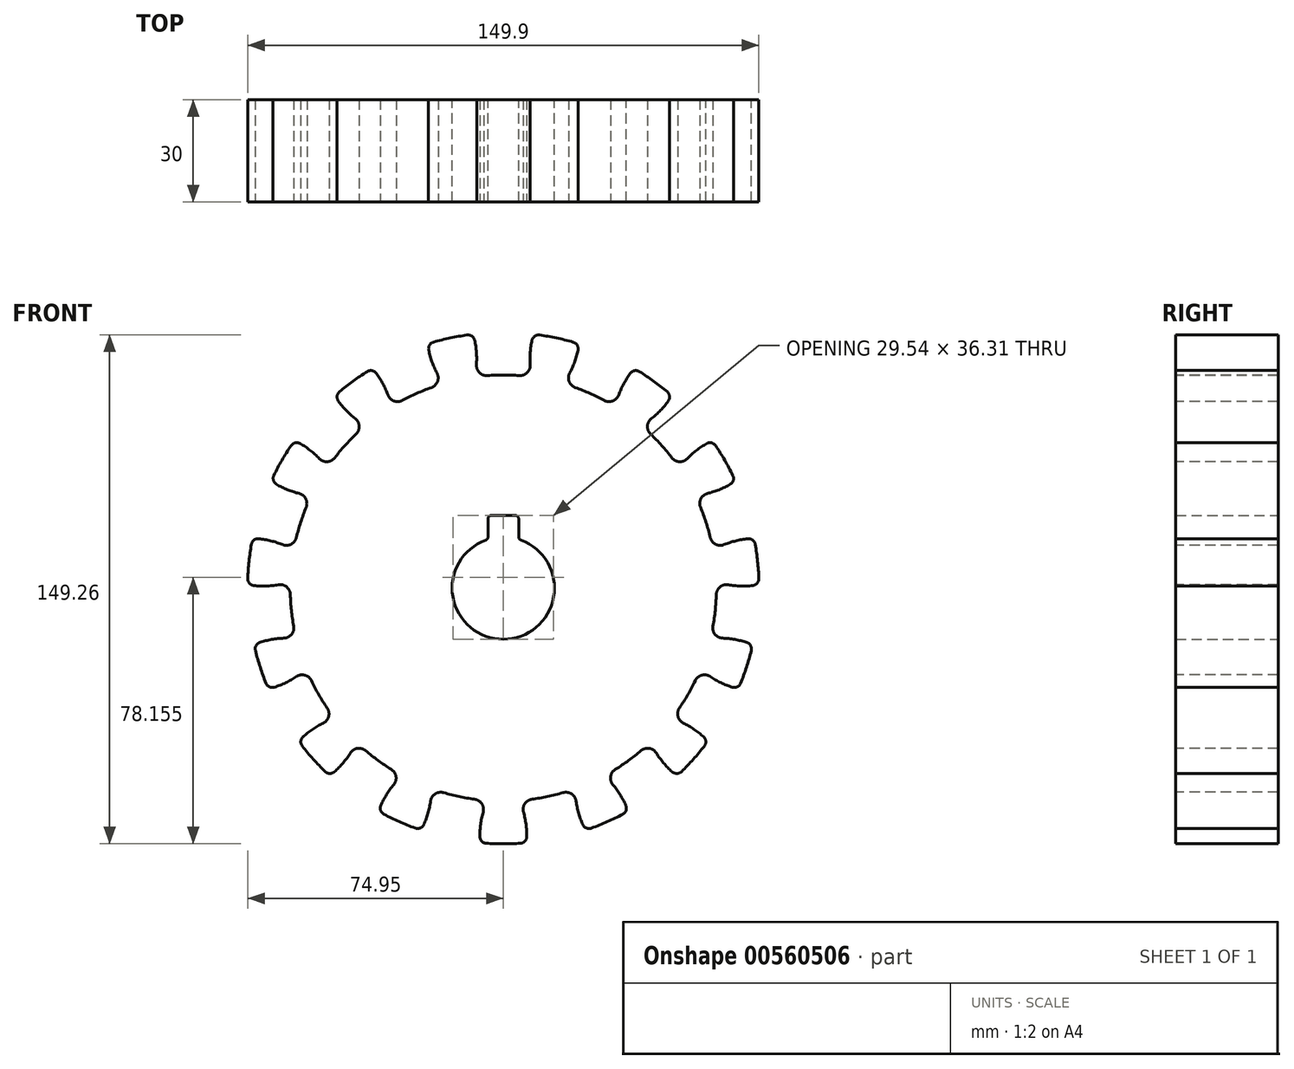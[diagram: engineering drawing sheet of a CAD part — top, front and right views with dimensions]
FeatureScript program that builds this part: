
annotation { "Feature Type Name" : "Feature", "Feature Type Description" : "" }
export const myFeature = defineFeature(function(context is Context, id is Id, definition is map)
    precondition{}
    {
        {
            var Q0;
            Q0=qCreatedBy(makeId("Front.planeOp"),FACE);
            var sketch = newSketch(context, id + "F0", { "sketchPlane" : qUnion([Q0])});
            skCircle(sketch, "E0", {"center": v(0, 0) * mm, "radius": 75 * mm});
            skArc(sketch, "E1", {"start": v(-5.16, 14.09) * mm, "mid": v(0, -15) * mm, "end": v(5.16, 14.09) * mm});
            skLineSegment(sketch, "E2.top", {"start": v(-3.5, 21.3) * mm, "end": v(3.5, 21.3) * mm});
            skLineSegment(sketch, "E2.left", {"start": v(-4.5, 15.02) * mm, "end": v(-4.5, 20.3) * mm});
            skLineSegment(sketch, "E2.right", {"start": v(4.5, 15.02) * mm, "end": v(4.5, 20.3) * mm});
            skPoint(sketch, "E3.visualSharp", {"position": v(-4.5, 21.3) * mm});
            skArc(sketch, "E3.filletArc", {"start": v(-3.5, 21.3) * mm, "mid": v(-4.2, 21.02) * mm, "end": v(-4.5, 20.3) * mm});
            skPoint(sketch, "E4.visualSharp", {"position": v(4.5, 21.3) * mm});
            skArc(sketch, "E4.filletArc", {"start": v(4.5, 20.3) * mm, "mid": v(4.2, 21.02) * mm, "end": v(3.5, 21.3) * mm});
            skPoint(sketch, "E5.visualSharp", {"position": v(4.5, 14.3) * mm});
            skArc(sketch, "E5.filletArc", {"start": v(4.5, 15.02) * mm, "mid": v(4.68, 14.45) * mm, "end": v(5.16, 14.09) * mm});
            skPoint(sketch, "E6.visualSharp", {"position": v(-4.5, 14.3) * mm});
            skArc(sketch, "E6.filletArc", {"start": v(-5.16, 14.09) * mm, "mid": v(-4.68, 14.45) * mm, "end": v(-4.5, 15.02) * mm});
            skSolve(sketch);
        }
        {
            var Q0;
            Q0 = qSketchRegion(id + "F0", true);
            extrude(context, id + "F1", {"entities" : qUnion([Q0]), "depth" : 30 * mm, "offsetDistance" : 25 * mm});
        }
        {
            var Q0;
            Q0=makeQuery(id+"F1.opExtrude","CAP_FACE",FACE,{"disambiguationData":[OSD([sQuery(id+"F0.wireOp",EDGE,"E0"),sQuery(id+"F0.wireOp",EDGE,"E1"),sQuery(id+"F0.wireOp",EDGE,"E2.top"),sQuery(id+"F0.wireOp",EDGE,"E2.left"),sQuery(id+"F0.wireOp",EDGE,"E2.right"),sQuery(id+"F0.wireOp",EDGE,"E3.filletArc"),sQuery(id+"F0.wireOp",EDGE,"E4.filletArc"),sQuery(id+"F0.wireOp",EDGE,"E5.filletArc"),sQuery(id+"F0.wireOp",EDGE,"E6.filletArc")])],"isStart":false});
            var sketch = newSketch(context, id + "F2", { "sketchPlane" : qUnion([Q0])});
            skArc(sketch, "E7", {"start": v(16.1, 86) * mm, "mid": v(0, 87.5) * mm, "end": v(-16.1, 86) * mm});
            skArc(sketch, "E8", {"start": v(4.66, 62.33) * mm, "mid": v(0, 62.5) * mm, "end": v(-4.66, 62.33) * mm});
            skPoint(sketch, "E9", {"position": v(0, 68.35) * mm});
            skArc(sketch, "E10", {"start": v(16.1, 86) * mm, "mid": v(9.63, 76.71) * mm, "end": v(7.88, 65.53) * mm});
            skArc(sketch, "E11.trimOffspring", {"start": v(-16.1, 86) * mm, "mid": v(-9.63, 76.71) * mm, "end": v(-7.88, 65.53) * mm});
            skPoint(sketch, "E12.visualSharp", {"position": v(-8.4, 61.93) * mm});
            skArc(sketch, "E12.filletArc", {"start": v(-7.88, 65.53) * mm, "mid": v(-7, 63.2) * mm, "end": v(-4.66, 62.33) * mm});
            skPoint(sketch, "E13.visualSharp", {"position": v(8.4, 61.93) * mm});
            skArc(sketch, "E13.filletArc", {"start": v(4.66, 62.33) * mm, "mid": v(7, 63.2) * mm, "end": v(7.88, 65.53) * mm});
            skArc(sketch, "E14.1.0", {"start": v(-20.28, 85.12) * mm, "mid": v(-35.59, 79.94) * mm, "end": v(-49.68, 72.03) * mm});
            skArc(sketch, "E14.1.1", {"start": v(-49.68, 72.03) * mm, "mid": v(-40, 66.16) * mm, "end": v(-33.85, 56.66) * mm});
            skArc(sketch, "E14.1.2", {"start": v(-20.28, 85.12) * mm, "mid": v(-22.4, 74) * mm, "end": v(-19.45, 63.07) * mm});
            skArc(sketch, "E14.1.3", {"start": v(-21.09, 58.83) * mm, "mid": v(-19.3, 60.58) * mm, "end": v(-19.45, 63.07) * mm});
            skArc(sketch, "E14.1.4", {"start": v(-21.09, 58.83) * mm, "mid": v(-25.42, 57.1) * mm, "end": v(-29.61, 55.04) * mm});
            skArc(sketch, "E14.1.5", {"start": v(-33.85, 56.66) * mm, "mid": v(-32.1, 54.88) * mm, "end": v(-29.61, 55.04) * mm});
            skArc(sketch, "E14.2.0", {"start": v(-53.15, 69.5) * mm, "mid": v(-65.03, 58.55) * mm, "end": v(-74.68, 45.6) * mm});
            skArc(sketch, "E14.2.1", {"start": v(-74.68, 45.6) * mm, "mid": v(-63.45, 44.17) * mm, "end": v(-53.97, 38) * mm});
            skArc(sketch, "E14.2.2", {"start": v(-53.15, 69.5) * mm, "mid": v(-50.56, 58.49) * mm, "end": v(-43.42, 49.7) * mm});
            skArc(sketch, "E14.2.3", {"start": v(-43.2, 45.17) * mm, "mid": v(-42.27, 47.49) * mm, "end": v(-43.42, 49.7) * mm});
            skArc(sketch, "E14.2.4", {"start": v(-43.2, 45.17) * mm, "mid": v(-46.45, 41.82) * mm, "end": v(-49.44, 38.24) * mm});
            skArc(sketch, "E14.2.5", {"start": v(-53.97, 38) * mm, "mid": v(-51.65, 37.08) * mm, "end": v(-49.44, 38.24) * mm});
            skArc(sketch, "E15.3.3.0", {"start": v(-76.82, 41.88) * mm, "mid": v(-83.22, 27.04) * mm, "end": v(-86.77, 11.27) * mm});
            skArc(sketch, "E15.4.3.0", {"start": v(-86.77, 11.27) * mm, "mid": v(-75.93, 14.54) * mm, "end": v(-64.76, 12.75) * mm});
            skArc(sketch, "E15.8.3.0", {"start": v(-76.82, 41.88) * mm, "mid": v(-69.98, 32.87) * mm, "end": v(-59.89, 27.74) * mm});
            skArc(sketch, "E15.12.3.0", {"start": v(-57.83, 23.7) * mm, "mid": v(-57.93, 26.19) * mm, "end": v(-59.89, 27.74) * mm});
            skArc(sketch, "E15.16.3.0", {"start": v(-57.83, 23.7) * mm, "mid": v(-59.44, 19.31) * mm, "end": v(-60.72, 14.82) * mm});
            skArc(sketch, "E15.20.3.0", {"start": v(-64.76, 12.75) * mm, "mid": v(-62.26, 12.87) * mm, "end": v(-60.72, 14.82) * mm});
            skArc(sketch, "E16.3.4.0", {"start": v(-87.22, 7.01) * mm, "mid": v(-87.02, -9.15) * mm, "end": v(-83.85, -25) * mm});
            skArc(sketch, "E16.4.4.0", {"start": v(-83.85, -25) * mm, "mid": v(-75.28, -17.6) * mm, "end": v(-64.35, -14.69) * mm});
            skArc(sketch, "E16.8.4.0", {"start": v(-87.22, 7.01) * mm, "mid": v(-77.3, 1.56) * mm, "end": v(-66, 0.99) * mm});
            skArc(sketch, "E16.12.4.0", {"start": v(-62.47, -1.88) * mm, "mid": v(-63.58, 0.36) * mm, "end": v(-66, 0.99) * mm});
            skArc(sketch, "E16.16.4.0", {"start": v(-62.47, -1.88) * mm, "mid": v(-62.16, -6.53) * mm, "end": v(-61.5, -11.15) * mm});
            skArc(sketch, "E16.20.4.0", {"start": v(-64.35, -14.69) * mm, "mid": v(-62.11, -13.57) * mm, "end": v(-61.5, -11.15) * mm});
            skArc(sketch, "E16.3.5.0", {"start": v(-82.53, -29.07) * mm, "mid": v(-75.78, -43.75) * mm, "end": v(-66.44, -56.94) * mm});
            skArc(sketch, "E16.4.5.0", {"start": v(-66.44, -56.94) * mm, "mid": v(-61.62, -46.7) * mm, "end": v(-52.8, -39.59) * mm});
            skArc(sketch, "E16.8.5.0", {"start": v(-82.53, -29.07) * mm, "mid": v(-71.25, -30.01) * mm, "end": v(-60.69, -25.94) * mm});
            skArc(sketch, "E16.12.5.0", {"start": v(-56.3, -27.12) * mm, "mid": v(-58.23, -25.53) * mm, "end": v(-60.69, -25.94) * mm});
            skArc(sketch, "E16.16.5.0", {"start": v(-56.3, -27.12) * mm, "mid": v(-54.13, -31.25) * mm, "end": v(-51.64, -35.2) * mm});
            skArc(sketch, "E16.20.5.0", {"start": v(-52.8, -39.59) * mm, "mid": v(-51.22, -37.66) * mm, "end": v(-51.64, -35.2) * mm});
            skArc(sketch, "E16.3.6.0", {"start": v(-63.57, -60.12) * mm, "mid": v(-51.43, -70.79) * mm, "end": v(-37.53, -79.04) * mm});
            skArc(sketch, "E16.4.6.0", {"start": v(-37.53, -79.04) * mm, "mid": v(-37.3, -67.72) * mm, "end": v(-32.14, -57.64) * mm});
            skArc(sketch, "E16.8.6.0", {"start": v(-63.57, -60.12) * mm, "mid": v(-52.88, -56.4) * mm, "end": v(-44.9, -48.38) * mm});
            skArc(sketch, "E16.12.6.0", {"start": v(-40.4, -47.68) * mm, "mid": v(-42.8, -47) * mm, "end": v(-44.9, -48.38) * mm});
            skArc(sketch, "E16.16.6.0", {"start": v(-40.4, -47.68) * mm, "mid": v(-36.74, -50.56) * mm, "end": v(-32.86, -53.16) * mm});
            skArc(sketch, "E16.20.6.0", {"start": v(-32.14, -57.64) * mm, "mid": v(-31.48, -55.24) * mm, "end": v(-32.86, -53.16) * mm});
            skArc(sketch, "E16.3.7.0", {"start": v(-33.62, -80.78) * mm, "mid": v(-18.2, -85.59) * mm, "end": v(-2.14, -87.47) * mm});
            skArc(sketch, "E16.4.7.0", {"start": v(-2.14, -87.47) * mm, "mid": v(-6.52, -77.04) * mm, "end": v(-5.92, -65.73) * mm});
            skArc(sketch, "E16.8.7.0", {"start": v(-33.62, -80.78) * mm, "mid": v(-25.37, -73.03) * mm, "end": v(-21.33, -62.46) * mm});
            skArc(sketch, "E16.12.7.0", {"start": v(-17.52, -60) * mm, "mid": v(-19.99, -60.35) * mm, "end": v(-21.33, -62.46) * mm});
            skArc(sketch, "E16.16.7.0", {"start": v(-17.52, -60) * mm, "mid": v(-13, -61.13) * mm, "end": v(-8.4, -61.93) * mm});
            skArc(sketch, "E16.20.7.0", {"start": v(-5.92, -65.73) * mm, "mid": v(-6.29, -63.27) * mm, "end": v(-8.4, -61.93) * mm});
            skArc(sketch, "E16.3.8.0", {"start": v(2.14, -87.47) * mm, "mid": v(18.2, -85.59) * mm, "end": v(33.62, -80.78) * mm});
            skArc(sketch, "E16.4.8.0", {"start": v(33.62, -80.78) * mm, "mid": v(25.37, -73.03) * mm, "end": v(21.33, -62.46) * mm});
            skArc(sketch, "E16.8.8.0", {"start": v(2.14, -87.47) * mm, "mid": v(6.52, -77.04) * mm, "end": v(5.92, -65.73) * mm});
            skArc(sketch, "E16.12.8.0", {"start": v(8.4, -61.93) * mm, "mid": v(6.29, -63.27) * mm, "end": v(5.92, -65.73) * mm});
            skArc(sketch, "E16.16.8.0", {"start": v(8.4, -61.93) * mm, "mid": v(13, -61.13) * mm, "end": v(17.52, -60) * mm});
            skArc(sketch, "E16.20.8.0", {"start": v(21.33, -62.46) * mm, "mid": v(19.99, -60.35) * mm, "end": v(17.52, -60) * mm});
            skArc(sketch, "E16.3.9.0", {"start": v(37.53, -79.04) * mm, "mid": v(51.43, -70.79) * mm, "end": v(63.57, -60.12) * mm});
            skArc(sketch, "E16.4.9.0", {"start": v(63.57, -60.12) * mm, "mid": v(52.88, -56.4) * mm, "end": v(44.9, -48.38) * mm});
            skArc(sketch, "E16.8.9.0", {"start": v(37.53, -79.04) * mm, "mid": v(37.3, -67.72) * mm, "end": v(32.14, -57.64) * mm});
            skArc(sketch, "E16.12.9.0", {"start": v(32.86, -53.16) * mm, "mid": v(31.48, -55.24) * mm, "end": v(32.14, -57.64) * mm});
            skArc(sketch, "E16.16.9.0", {"start": v(32.86, -53.16) * mm, "mid": v(36.74, -50.56) * mm, "end": v(40.4, -47.68) * mm});
            skArc(sketch, "E16.20.9.0", {"start": v(44.9, -48.38) * mm, "mid": v(42.8, -47) * mm, "end": v(40.4, -47.68) * mm});
            skArc(sketch, "E16.3.10.0", {"start": v(66.44, -56.94) * mm, "mid": v(75.78, -43.75) * mm, "end": v(82.53, -29.07) * mm});
            skArc(sketch, "E16.4.10.0", {"start": v(82.53, -29.07) * mm, "mid": v(71.25, -30.01) * mm, "end": v(60.69, -25.94) * mm});
            skArc(sketch, "E16.8.10.0", {"start": v(66.44, -56.94) * mm, "mid": v(61.62, -46.7) * mm, "end": v(52.8, -39.59) * mm});
            skArc(sketch, "E16.12.10.0", {"start": v(51.64, -35.2) * mm, "mid": v(51.22, -37.66) * mm, "end": v(52.8, -39.59) * mm});
            skArc(sketch, "E16.16.10.0", {"start": v(51.64, -35.2) * mm, "mid": v(54.13, -31.25) * mm, "end": v(56.3, -27.12) * mm});
            skArc(sketch, "E16.20.10.0", {"start": v(60.69, -25.94) * mm, "mid": v(58.23, -25.53) * mm, "end": v(56.3, -27.12) * mm});
            skArc(sketch, "E16.3.11.0", {"start": v(83.85, -25) * mm, "mid": v(87.02, -9.15) * mm, "end": v(87.22, 7.01) * mm});
            skArc(sketch, "E16.4.11.0", {"start": v(87.22, 7.01) * mm, "mid": v(77.3, 1.56) * mm, "end": v(66, 0.99) * mm});
            skArc(sketch, "E16.8.11.0", {"start": v(83.85, -25) * mm, "mid": v(75.28, -17.6) * mm, "end": v(64.35, -14.69) * mm});
            skArc(sketch, "E16.12.11.0", {"start": v(61.5, -11.15) * mm, "mid": v(62.11, -13.57) * mm, "end": v(64.35, -14.69) * mm});
            skArc(sketch, "E16.16.11.0", {"start": v(61.5, -11.15) * mm, "mid": v(62.16, -6.53) * mm, "end": v(62.47, -1.88) * mm});
            skArc(sketch, "E16.20.11.0", {"start": v(66, 0.99) * mm, "mid": v(63.58, 0.36) * mm, "end": v(62.47, -1.88) * mm});
            skArc(sketch, "E16.3.12.0", {"start": v(86.77, 11.27) * mm, "mid": v(83.22, 27.04) * mm, "end": v(76.82, 41.88) * mm});
            skArc(sketch, "E16.4.12.0", {"start": v(76.82, 41.88) * mm, "mid": v(69.98, 32.87) * mm, "end": v(59.89, 27.74) * mm});
            skArc(sketch, "E16.8.12.0", {"start": v(86.77, 11.27) * mm, "mid": v(75.93, 14.54) * mm, "end": v(64.76, 12.75) * mm});
            skArc(sketch, "E16.12.12.0", {"start": v(60.72, 14.82) * mm, "mid": v(62.26, 12.87) * mm, "end": v(64.76, 12.75) * mm});
            skArc(sketch, "E16.16.12.0", {"start": v(60.72, 14.82) * mm, "mid": v(59.44, 19.31) * mm, "end": v(57.83, 23.7) * mm});
            skArc(sketch, "E16.20.12.0", {"start": v(59.89, 27.74) * mm, "mid": v(57.93, 26.19) * mm, "end": v(57.83, 23.7) * mm});
            skArc(sketch, "E16.3.13.0", {"start": v(74.68, 45.6) * mm, "mid": v(65.03, 58.55) * mm, "end": v(53.15, 69.5) * mm});
            skArc(sketch, "E16.4.13.0", {"start": v(53.15, 69.5) * mm, "mid": v(50.56, 58.49) * mm, "end": v(43.42, 49.7) * mm});
            skArc(sketch, "E16.8.13.0", {"start": v(74.68, 45.6) * mm, "mid": v(63.45, 44.17) * mm, "end": v(53.97, 38) * mm});
            skArc(sketch, "E16.12.13.0", {"start": v(49.44, 38.24) * mm, "mid": v(51.65, 37.08) * mm, "end": v(53.97, 38) * mm});
            skArc(sketch, "E16.16.13.0", {"start": v(49.44, 38.24) * mm, "mid": v(46.45, 41.82) * mm, "end": v(43.2, 45.17) * mm});
            skArc(sketch, "E16.20.13.0", {"start": v(43.42, 49.7) * mm, "mid": v(42.27, 47.49) * mm, "end": v(43.2, 45.17) * mm});
            skArc(sketch, "E16.3.14.0", {"start": v(49.68, 72.03) * mm, "mid": v(35.59, 79.94) * mm, "end": v(20.28, 85.12) * mm});
            skArc(sketch, "E16.4.14.0", {"start": v(20.28, 85.12) * mm, "mid": v(22.4, 74) * mm, "end": v(19.45, 63.07) * mm});
            skArc(sketch, "E16.8.14.0", {"start": v(49.68, 72.03) * mm, "mid": v(40, 66.16) * mm, "end": v(33.85, 56.66) * mm});
            skArc(sketch, "E16.12.14.0", {"start": v(29.61, 55.04) * mm, "mid": v(32.1, 54.88) * mm, "end": v(33.85, 56.66) * mm});
            skArc(sketch, "E16.16.14.0", {"start": v(29.61, 55.04) * mm, "mid": v(25.42, 57.1) * mm, "end": v(21.09, 58.83) * mm});
            skArc(sketch, "E16.20.14.0", {"start": v(19.45, 63.07) * mm, "mid": v(19.3, 60.58) * mm, "end": v(21.09, 58.83) * mm});
            skSolve(sketch);
        }
        {
            var Q0;
            Q0 = qSketchRegion(id + "F2", true);
            extrude(context, id + "F3", {"entities" : qUnion([Q0]), "operationType" : NewBodyOperationType.REMOVE, "oppositeDirection" : true, "depth" : 31 * mm, "offsetDistance" : 25 * mm});
        }
        {
            var Q0;
            Q0=makeQuery(id+"F3.boolean.opBoolean","INTERSECT",EDGE,{"derivedFrom":[makeQuery(id+"F1.opExtrude","SWEPT_FACE",FACE,{"disambiguationData":[OSD([sQuery(id+"F0.wireOp",EDGE,"E0")])]}),makeQuery(id+"F3.opExtrude","SWEPT_FACE",FACE,{"disambiguationData":[OSD([sQuery(id+"F2.wireOp",EDGE,"E16.4.12.0")])]})]});
            var Q1;
            Q1=makeQuery(id+"F3.boolean.opBoolean","INTERSECT",EDGE,{"derivedFrom":[makeQuery(id+"F1.opExtrude","SWEPT_FACE",FACE,{"disambiguationData":[OSD([sQuery(id+"F0.wireOp",EDGE,"E0")])]}),makeQuery(id+"F3.opExtrude","SWEPT_FACE",FACE,{"disambiguationData":[OSD([sQuery(id+"F2.wireOp",EDGE,"E16.8.13.0")])]})]});
            var Q2;
            Q2=makeQuery(id+"F3.boolean.opBoolean","INTERSECT",EDGE,{"derivedFrom":[makeQuery(id+"F1.opExtrude","SWEPT_FACE",FACE,{"disambiguationData":[OSD([sQuery(id+"F0.wireOp",EDGE,"E0")])]}),makeQuery(id+"F3.opExtrude","SWEPT_FACE",FACE,{"disambiguationData":[OSD([sQuery(id+"F2.wireOp",EDGE,"E16.4.13.0")])]})]});
            var Q3;
            Q3=makeQuery(id+"F3.boolean.opBoolean","INTERSECT",EDGE,{"derivedFrom":[makeQuery(id+"F1.opExtrude","SWEPT_FACE",FACE,{"disambiguationData":[OSD([sQuery(id+"F0.wireOp",EDGE,"E0")])]}),makeQuery(id+"F3.opExtrude","SWEPT_FACE",FACE,{"disambiguationData":[OSD([sQuery(id+"F2.wireOp",EDGE,"E16.8.14.0")])]})]});
            var Q4;
            Q4=makeQuery(id+"F3.boolean.opBoolean","INTERSECT",EDGE,{"derivedFrom":[makeQuery(id+"F1.opExtrude","SWEPT_FACE",FACE,{"disambiguationData":[OSD([sQuery(id+"F0.wireOp",EDGE,"E0")])]}),makeQuery(id+"F3.opExtrude","SWEPT_FACE",FACE,{"disambiguationData":[OSD([sQuery(id+"F2.wireOp",EDGE,"E16.4.14.0")])]})]});
            var Q5;
            Q5=makeQuery(id+"F3.boolean.opBoolean","INTERSECT",EDGE,{"derivedFrom":[makeQuery(id+"F1.opExtrude","SWEPT_FACE",FACE,{"disambiguationData":[OSD([sQuery(id+"F0.wireOp",EDGE,"E0")])]}),makeQuery(id+"F3.opExtrude","SWEPT_FACE",FACE,{"disambiguationData":[OSD([sQuery(id+"F2.wireOp",EDGE,"E10")])]})]});
            var Q6;
            Q6=makeQuery(id+"F3.boolean.opBoolean","INTERSECT",EDGE,{"derivedFrom":[makeQuery(id+"F1.opExtrude","SWEPT_FACE",FACE,{"disambiguationData":[OSD([sQuery(id+"F0.wireOp",EDGE,"E0")])]}),makeQuery(id+"F3.opExtrude","SWEPT_FACE",FACE,{"disambiguationData":[OSD([sQuery(id+"F2.wireOp",EDGE,"E11.trimOffspring")])]})]});
            var Q7;
            Q7=makeQuery(id+"F3.boolean.opBoolean","INTERSECT",EDGE,{"derivedFrom":[makeQuery(id+"F1.opExtrude","SWEPT_FACE",FACE,{"disambiguationData":[OSD([sQuery(id+"F0.wireOp",EDGE,"E0")])]}),makeQuery(id+"F3.opExtrude","SWEPT_FACE",FACE,{"disambiguationData":[OSD([sQuery(id+"F2.wireOp",EDGE,"E14.1.2")])]})]});
            var Q8;
            Q8=makeQuery(id+"F3.boolean.opBoolean","INTERSECT",EDGE,{"derivedFrom":[makeQuery(id+"F1.opExtrude","SWEPT_FACE",FACE,{"disambiguationData":[OSD([sQuery(id+"F0.wireOp",EDGE,"E0")])]}),makeQuery(id+"F3.opExtrude","SWEPT_FACE",FACE,{"disambiguationData":[OSD([sQuery(id+"F2.wireOp",EDGE,"E14.1.1")])]})]});
            var Q9;
            Q9=makeQuery(id+"F3.boolean.opBoolean","INTERSECT",EDGE,{"derivedFrom":[makeQuery(id+"F1.opExtrude","SWEPT_FACE",FACE,{"disambiguationData":[OSD([sQuery(id+"F0.wireOp",EDGE,"E0")])]}),makeQuery(id+"F3.opExtrude","SWEPT_FACE",FACE,{"disambiguationData":[OSD([sQuery(id+"F2.wireOp",EDGE,"E14.2.2")])]})]});
            var Q10;
            Q10=makeQuery(id+"F3.boolean.opBoolean","INTERSECT",EDGE,{"derivedFrom":[makeQuery(id+"F1.opExtrude","SWEPT_FACE",FACE,{"disambiguationData":[OSD([sQuery(id+"F0.wireOp",EDGE,"E0")])]}),makeQuery(id+"F3.opExtrude","SWEPT_FACE",FACE,{"disambiguationData":[OSD([sQuery(id+"F2.wireOp",EDGE,"E14.2.1")])]})]});
            var Q11;
            Q11=makeQuery(id+"F3.boolean.opBoolean","INTERSECT",EDGE,{"derivedFrom":[makeQuery(id+"F1.opExtrude","SWEPT_FACE",FACE,{"disambiguationData":[OSD([sQuery(id+"F0.wireOp",EDGE,"E0")])]}),makeQuery(id+"F3.opExtrude","SWEPT_FACE",FACE,{"disambiguationData":[OSD([sQuery(id+"F2.wireOp",EDGE,"E15.8.3.0")])]})]});
            var Q12;
            Q12=makeQuery(id+"F3.boolean.opBoolean","INTERSECT",EDGE,{"derivedFrom":[makeQuery(id+"F1.opExtrude","SWEPT_FACE",FACE,{"disambiguationData":[OSD([sQuery(id+"F0.wireOp",EDGE,"E0")])]}),makeQuery(id+"F3.opExtrude","SWEPT_FACE",FACE,{"disambiguationData":[OSD([sQuery(id+"F2.wireOp",EDGE,"E15.4.3.0")])]})]});
            var Q13;
            Q13=makeQuery(id+"F3.boolean.opBoolean","INTERSECT",EDGE,{"derivedFrom":[makeQuery(id+"F1.opExtrude","SWEPT_FACE",FACE,{"disambiguationData":[OSD([sQuery(id+"F0.wireOp",EDGE,"E0")])]}),makeQuery(id+"F3.opExtrude","SWEPT_FACE",FACE,{"disambiguationData":[OSD([sQuery(id+"F2.wireOp",EDGE,"E16.8.4.0")])]})]});
            var Q14;
            Q14=makeQuery(id+"F3.boolean.opBoolean","INTERSECT",EDGE,{"derivedFrom":[makeQuery(id+"F1.opExtrude","SWEPT_FACE",FACE,{"disambiguationData":[OSD([sQuery(id+"F0.wireOp",EDGE,"E0")])]}),makeQuery(id+"F3.opExtrude","SWEPT_FACE",FACE,{"disambiguationData":[OSD([sQuery(id+"F2.wireOp",EDGE,"E16.4.4.0")])]})]});
            var Q15;
            Q15=makeQuery(id+"F3.boolean.opBoolean","INTERSECT",EDGE,{"derivedFrom":[makeQuery(id+"F1.opExtrude","SWEPT_FACE",FACE,{"disambiguationData":[OSD([sQuery(id+"F0.wireOp",EDGE,"E0")])]}),makeQuery(id+"F3.opExtrude","SWEPT_FACE",FACE,{"disambiguationData":[OSD([sQuery(id+"F2.wireOp",EDGE,"E16.8.5.0")])]})]});
            var Q16;
            Q16=makeQuery(id+"F3.boolean.opBoolean","INTERSECT",EDGE,{"derivedFrom":[makeQuery(id+"F1.opExtrude","SWEPT_FACE",FACE,{"disambiguationData":[OSD([sQuery(id+"F0.wireOp",EDGE,"E0")])]}),makeQuery(id+"F3.opExtrude","SWEPT_FACE",FACE,{"disambiguationData":[OSD([sQuery(id+"F2.wireOp",EDGE,"E16.4.5.0")])]})]});
            var Q17;
            Q17=makeQuery(id+"F3.boolean.opBoolean","INTERSECT",EDGE,{"derivedFrom":[makeQuery(id+"F1.opExtrude","SWEPT_FACE",FACE,{"disambiguationData":[OSD([sQuery(id+"F0.wireOp",EDGE,"E0")])]}),makeQuery(id+"F3.opExtrude","SWEPT_FACE",FACE,{"disambiguationData":[OSD([sQuery(id+"F2.wireOp",EDGE,"E16.8.6.0")])]})]});
            var Q18;
            Q18=makeQuery(id+"F3.boolean.opBoolean","INTERSECT",EDGE,{"derivedFrom":[makeQuery(id+"F1.opExtrude","SWEPT_FACE",FACE,{"disambiguationData":[OSD([sQuery(id+"F0.wireOp",EDGE,"E0")])]}),makeQuery(id+"F3.opExtrude","SWEPT_FACE",FACE,{"disambiguationData":[OSD([sQuery(id+"F2.wireOp",EDGE,"E16.4.6.0")])]})]});
            var Q19;
            Q19=makeQuery(id+"F3.boolean.opBoolean","INTERSECT",EDGE,{"derivedFrom":[makeQuery(id+"F1.opExtrude","SWEPT_FACE",FACE,{"disambiguationData":[OSD([sQuery(id+"F0.wireOp",EDGE,"E0")])]}),makeQuery(id+"F3.opExtrude","SWEPT_FACE",FACE,{"disambiguationData":[OSD([sQuery(id+"F2.wireOp",EDGE,"E16.8.7.0")])]})]});
            var Q20;
            Q20=makeQuery(id+"F3.boolean.opBoolean","INTERSECT",EDGE,{"derivedFrom":[makeQuery(id+"F1.opExtrude","SWEPT_FACE",FACE,{"disambiguationData":[OSD([sQuery(id+"F0.wireOp",EDGE,"E0")])]}),makeQuery(id+"F3.opExtrude","SWEPT_FACE",FACE,{"disambiguationData":[OSD([sQuery(id+"F2.wireOp",EDGE,"E16.4.7.0")])]})]});
            var Q21;
            Q21=makeQuery(id+"F3.boolean.opBoolean","INTERSECT",EDGE,{"derivedFrom":[makeQuery(id+"F1.opExtrude","SWEPT_FACE",FACE,{"disambiguationData":[OSD([sQuery(id+"F0.wireOp",EDGE,"E0")])]}),makeQuery(id+"F3.opExtrude","SWEPT_FACE",FACE,{"disambiguationData":[OSD([sQuery(id+"F2.wireOp",EDGE,"E16.8.8.0")])]})]});
            var Q22;
            Q22=makeQuery(id+"F3.boolean.opBoolean","INTERSECT",EDGE,{"derivedFrom":[makeQuery(id+"F1.opExtrude","SWEPT_FACE",FACE,{"disambiguationData":[OSD([sQuery(id+"F0.wireOp",EDGE,"E0")])]}),makeQuery(id+"F3.opExtrude","SWEPT_FACE",FACE,{"disambiguationData":[OSD([sQuery(id+"F2.wireOp",EDGE,"E16.4.8.0")])]})]});
            var Q23;
            Q23=makeQuery(id+"F3.boolean.opBoolean","INTERSECT",EDGE,{"derivedFrom":[makeQuery(id+"F1.opExtrude","SWEPT_FACE",FACE,{"disambiguationData":[OSD([sQuery(id+"F0.wireOp",EDGE,"E0")])]}),makeQuery(id+"F3.opExtrude","SWEPT_FACE",FACE,{"disambiguationData":[OSD([sQuery(id+"F2.wireOp",EDGE,"E16.8.9.0")])]})]});
            var Q24;
            Q24=makeQuery(id+"F3.boolean.opBoolean","INTERSECT",EDGE,{"derivedFrom":[makeQuery(id+"F1.opExtrude","SWEPT_FACE",FACE,{"disambiguationData":[OSD([sQuery(id+"F0.wireOp",EDGE,"E0")])]}),makeQuery(id+"F3.opExtrude","SWEPT_FACE",FACE,{"disambiguationData":[OSD([sQuery(id+"F2.wireOp",EDGE,"E16.4.9.0")])]})]});
            var Q25;
            Q25=makeQuery(id+"F3.boolean.opBoolean","INTERSECT",EDGE,{"derivedFrom":[makeQuery(id+"F1.opExtrude","SWEPT_FACE",FACE,{"disambiguationData":[OSD([sQuery(id+"F0.wireOp",EDGE,"E0")])]}),makeQuery(id+"F3.opExtrude","SWEPT_FACE",FACE,{"disambiguationData":[OSD([sQuery(id+"F2.wireOp",EDGE,"E16.8.10.0")])]})]});
            var Q26;
            Q26=makeQuery(id+"F3.boolean.opBoolean","INTERSECT",EDGE,{"derivedFrom":[makeQuery(id+"F1.opExtrude","SWEPT_FACE",FACE,{"disambiguationData":[OSD([sQuery(id+"F0.wireOp",EDGE,"E0")])]}),makeQuery(id+"F3.opExtrude","SWEPT_FACE",FACE,{"disambiguationData":[OSD([sQuery(id+"F2.wireOp",EDGE,"E16.4.10.0")])]})]});
            var Q27;
            Q27=makeQuery(id+"F3.boolean.opBoolean","INTERSECT",EDGE,{"derivedFrom":[makeQuery(id+"F1.opExtrude","SWEPT_FACE",FACE,{"disambiguationData":[OSD([sQuery(id+"F0.wireOp",EDGE,"E0")])]}),makeQuery(id+"F3.opExtrude","SWEPT_FACE",FACE,{"disambiguationData":[OSD([sQuery(id+"F2.wireOp",EDGE,"E16.8.11.0")])]})]});
            var Q28;
            Q28=makeQuery(id+"F3.boolean.opBoolean","INTERSECT",EDGE,{"derivedFrom":[makeQuery(id+"F1.opExtrude","SWEPT_FACE",FACE,{"disambiguationData":[OSD([sQuery(id+"F0.wireOp",EDGE,"E0")])]}),makeQuery(id+"F3.opExtrude","SWEPT_FACE",FACE,{"disambiguationData":[OSD([sQuery(id+"F2.wireOp",EDGE,"E16.8.12.0")])]})]});
            var Q29;
            Q29=makeQuery(id+"F3.boolean.opBoolean","INTERSECT",EDGE,{"derivedFrom":[makeQuery(id+"F1.opExtrude","SWEPT_FACE",FACE,{"disambiguationData":[OSD([sQuery(id+"F0.wireOp",EDGE,"E0")])]}),makeQuery(id+"F3.opExtrude","SWEPT_FACE",FACE,{"disambiguationData":[OSD([sQuery(id+"F2.wireOp",EDGE,"E16.4.11.0")])]})]});
            fillet(context, id + "F4", {"entities" : qUnion([Q0, Q1, Q2, Q3, Q4, Q5, Q6, Q7, Q8, Q9, Q10, Q11, Q12, Q13, Q14, Q15, Q16, Q17, Q18, Q19, Q20, Q21, Q22, Q23, Q24, Q25, Q26, Q27, Q28, Q29]), "radius" : 2 * mm, "tangentPropagation" : true, "allowEdgeOverflow" : false});
        }
    });
